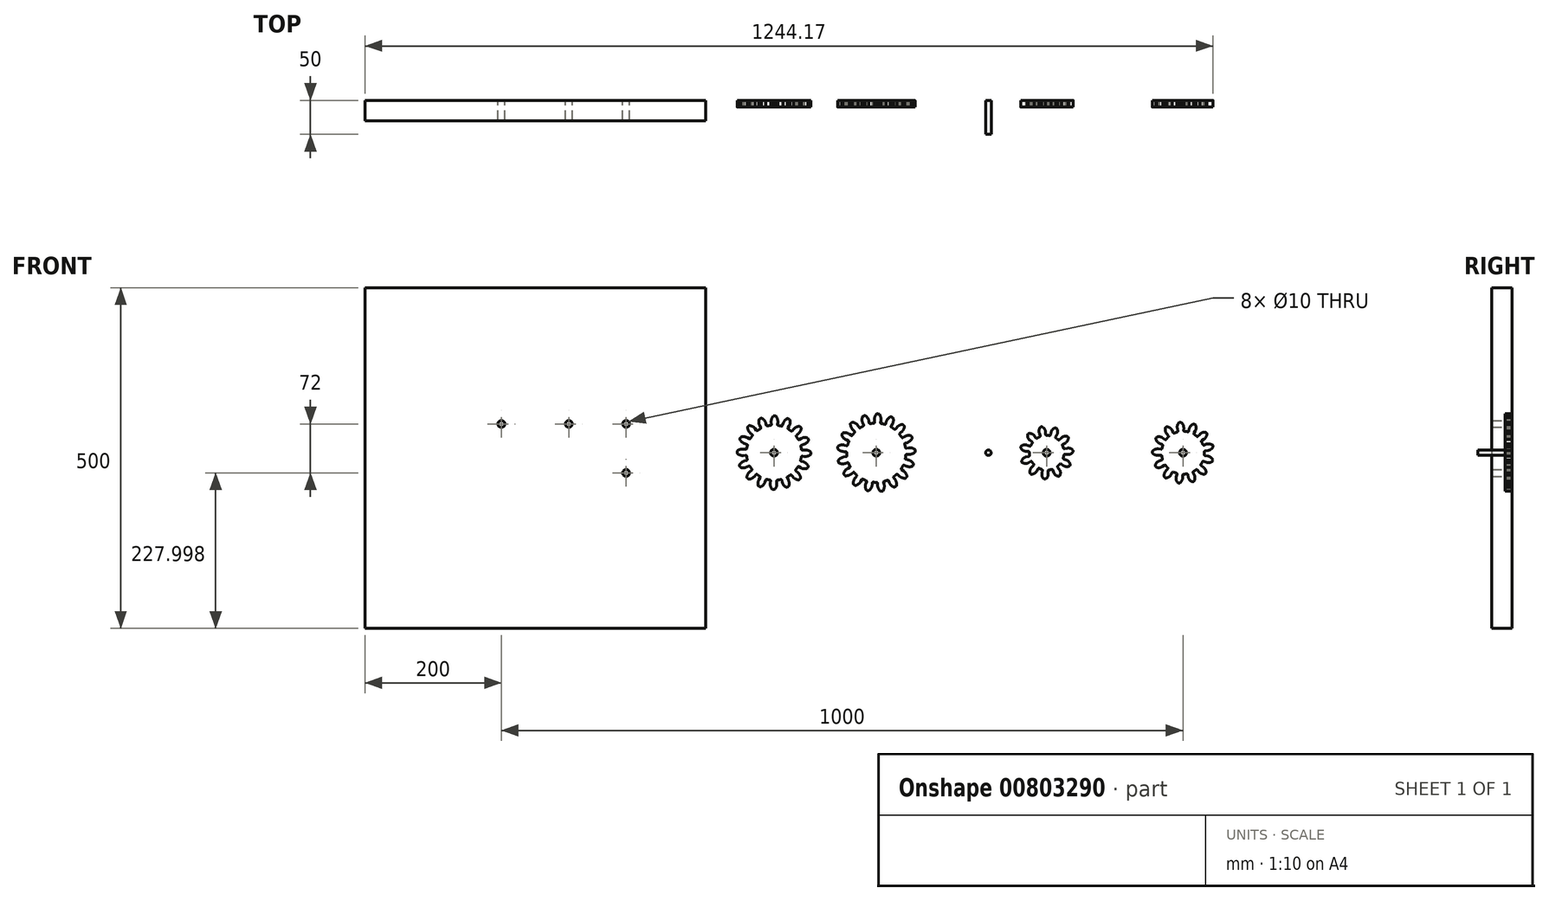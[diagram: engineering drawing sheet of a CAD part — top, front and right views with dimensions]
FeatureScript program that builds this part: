
annotation { "Feature Type Name" : "Feature", "Feature Type Description" : "" }
export const myFeature = defineFeature(function(context is Context, id is Id, definition is map)
    precondition{}
    {
        {
            var Q0;
            Q0=qCreatedBy(makeId("Front.planeOp"),FACE);
            var sketch = newSketch(context, id + "F0", { "sketchPlane" : qUnion([Q0])});
            skArc(sketch, "E0.0", {"start": v(-18.3, 50.8) * mm, "mid": v(-19.94, 50.18) * mm, "end": v(-21.55, 49.51) * mm});
            skPoint(sketch, "E1", {"position": v(11.62, 45) * mm});
            skArc(sketch, "E2", {"start": v(21.97, 38.92) * mm, "mid": v(23.56, 43.79) * mm, "end": v(22.98, 48.87) * mm});
            skPoint(sketch, "E3", {"position": v(22.98, 48.87) * mm});
            skPoint(sketch, "E4", {"position": v(22.17, 39.28) * mm});
            skLineSegment(sketch, "E5", {"start": v(22.17, 39.28) * mm, "end": v(20.49, 36.3) * mm});
            skPoint(sketch, "E6.visualSharp", {"position": v(19.9, 35.27) * mm});
            skArc(sketch, "E6.filletArc", {"start": v(20.49, 36.3) * mm, "mid": v(20.37, 35.4) * mm, "end": v(20.91, 34.68) * mm});
            skArc(sketch, "E7.1.0", {"start": v(5.4, 44.37) * mm, "mid": v(5, 49.47) * mm, "end": v(2.53, 53.94) * mm});
            skLineSegment(sketch, "E7.1.1", {"start": v(5.45, 44.77) * mm, "end": v(5.04, 41.38) * mm});
            skArc(sketch, "E7.1.2", {"start": v(5.04, 41.38) * mm, "mid": v(5.27, 40.5) * mm, "end": v(6.05, 40.05) * mm});
            skArc(sketch, "E7.2.0", {"start": v(-12, 43.06) * mm, "mid": v(-14.3, 47.62) * mm, "end": v(-18.3, 50.8) * mm});
            skLineSegment(sketch, "E7.2.1", {"start": v(-12.1, 43.45) * mm, "end": v(-11.18, 40.15) * mm});
            skArc(sketch, "E7.2.2", {"start": v(-11.18, 40.15) * mm, "mid": v(-10.63, 39.44) * mm, "end": v(-9.74, 39.31) * mm});
            skArc(sketch, "E7.3.0", {"start": v(-27.56, 35.2) * mm, "mid": v(-31.44, 38.52) * mm, "end": v(-36.35, 39.93) * mm});
            skLineSegment(sketch, "E7.3.1", {"start": v(-27.8, 35.51) * mm, "end": v(-25.7, 32.82) * mm});
            skArc(sketch, "E7.3.2", {"start": v(-25.7, 32.82) * mm, "mid": v(-24.91, 32.37) * mm, "end": v(-24.04, 32.6) * mm});
            skArc(sketch, "E7.4.0", {"start": v(-38.92, 21.97) * mm, "mid": v(-43.79, 23.56) * mm, "end": v(-48.87, 22.98) * mm});
            skLineSegment(sketch, "E7.4.1", {"start": v(-39.28, 22.17) * mm, "end": v(-36.3, 20.49) * mm});
            skArc(sketch, "E7.4.2", {"start": v(-36.3, 20.49) * mm, "mid": v(-35.4, 20.37) * mm, "end": v(-34.68, 20.91) * mm});
            skArc(sketch, "E7.5.0", {"start": v(-44.37, 5.4) * mm, "mid": v(-49.47, 5) * mm, "end": v(-53.94, 2.53) * mm});
            skLineSegment(sketch, "E7.5.1", {"start": v(-44.77, 5.45) * mm, "end": v(-41.38, 5.04) * mm});
            skArc(sketch, "E7.5.2", {"start": v(-41.38, 5.04) * mm, "mid": v(-40.5, 5.27) * mm, "end": v(-40.05, 6.05) * mm});
            skArc(sketch, "E7.6.0", {"start": v(-43.06, -12) * mm, "mid": v(-47.62, -14.3) * mm, "end": v(-50.8, -18.3) * mm});
            skLineSegment(sketch, "E7.6.1", {"start": v(-43.45, -12.1) * mm, "end": v(-40.15, -11.18) * mm});
            skArc(sketch, "E7.6.2", {"start": v(-40.15, -11.18) * mm, "mid": v(-39.44, -10.63) * mm, "end": v(-39.31, -9.74) * mm});
            skArc(sketch, "E7.7.0", {"start": v(-35.2, -27.56) * mm, "mid": v(-38.52, -31.44) * mm, "end": v(-39.93, -36.35) * mm});
            skLineSegment(sketch, "E7.7.1", {"start": v(-35.51, -27.8) * mm, "end": v(-32.82, -25.7) * mm});
            skArc(sketch, "E7.7.2", {"start": v(-32.82, -25.7) * mm, "mid": v(-32.37, -24.91) * mm, "end": v(-32.6, -24.04) * mm});
            skArc(sketch, "E7.8.0", {"start": v(-21.97, -38.92) * mm, "mid": v(-23.56, -43.79) * mm, "end": v(-22.98, -48.87) * mm});
            skLineSegment(sketch, "E7.8.1", {"start": v(-22.17, -39.28) * mm, "end": v(-20.49, -36.3) * mm});
            skArc(sketch, "E7.8.2", {"start": v(-20.49, -36.3) * mm, "mid": v(-20.37, -35.4) * mm, "end": v(-20.91, -34.68) * mm});
            skArc(sketch, "E7.9.0", {"start": v(-5.4, -44.37) * mm, "mid": v(-5, -49.47) * mm, "end": v(-2.53, -53.94) * mm});
            skLineSegment(sketch, "E7.9.1", {"start": v(-5.45, -44.77) * mm, "end": v(-5.04, -41.38) * mm});
            skArc(sketch, "E7.9.2", {"start": v(-5.04, -41.38) * mm, "mid": v(-5.27, -40.5) * mm, "end": v(-6.05, -40.05) * mm});
            skArc(sketch, "E7.10.0", {"start": v(12, -43.06) * mm, "mid": v(14.3, -47.62) * mm, "end": v(18.3, -50.8) * mm});
            skLineSegment(sketch, "E7.10.1", {"start": v(12.1, -43.45) * mm, "end": v(11.18, -40.15) * mm});
            skArc(sketch, "E7.10.2", {"start": v(11.18, -40.15) * mm, "mid": v(10.63, -39.44) * mm, "end": v(9.74, -39.31) * mm});
            skArc(sketch, "E7.11.0", {"start": v(27.56, -35.2) * mm, "mid": v(31.44, -38.52) * mm, "end": v(36.35, -39.93) * mm});
            skLineSegment(sketch, "E7.11.1", {"start": v(27.8, -35.51) * mm, "end": v(25.7, -32.82) * mm});
            skArc(sketch, "E7.11.2", {"start": v(25.7, -32.82) * mm, "mid": v(24.91, -32.37) * mm, "end": v(24.04, -32.6) * mm});
            skArc(sketch, "E7.12.0", {"start": v(38.92, -21.97) * mm, "mid": v(43.79, -23.56) * mm, "end": v(48.87, -22.98) * mm});
            skLineSegment(sketch, "E7.12.1", {"start": v(39.28, -22.17) * mm, "end": v(36.3, -20.49) * mm});
            skArc(sketch, "E7.12.2", {"start": v(36.3, -20.49) * mm, "mid": v(35.4, -20.37) * mm, "end": v(34.68, -20.91) * mm});
            skArc(sketch, "E7.13.0", {"start": v(44.37, -5.4) * mm, "mid": v(49.47, -5) * mm, "end": v(53.94, -2.53) * mm});
            skLineSegment(sketch, "E7.13.1", {"start": v(44.77, -5.45) * mm, "end": v(41.38, -5.04) * mm});
            skArc(sketch, "E7.13.2", {"start": v(41.38, -5.04) * mm, "mid": v(40.5, -5.27) * mm, "end": v(40.05, -6.05) * mm});
            skArc(sketch, "E7.14.0", {"start": v(43.06, 12) * mm, "mid": v(47.62, 14.3) * mm, "end": v(50.8, 18.3) * mm});
            skLineSegment(sketch, "E7.14.1", {"start": v(43.45, 12.1) * mm, "end": v(40.15, 11.18) * mm});
            skArc(sketch, "E7.14.2", {"start": v(40.15, 11.18) * mm, "mid": v(39.44, 10.63) * mm, "end": v(39.31, 9.74) * mm});
            skArc(sketch, "E7.15.0", {"start": v(35.2, 27.56) * mm, "mid": v(38.52, 31.44) * mm, "end": v(39.93, 36.35) * mm});
            skLineSegment(sketch, "E7.15.1", {"start": v(35.51, 27.8) * mm, "end": v(32.82, 25.7) * mm});
            skArc(sketch, "E7.15.2", {"start": v(32.82, 25.7) * mm, "mid": v(32.37, 24.91) * mm, "end": v(32.6, 24.04) * mm});
            skPoint(sketch, "E8", {"position": v(30.99, 36.66) * mm});
            skLineSegment(sketch, "E9", {"start": v(0, 0) * mm, "end": v(34.43, 33.45) * mm, "construction": true});
            skArc(sketch, "E10.MirrorCS", {"start": v(28.56, 34.38) * mm, "mid": v(32.54, 37.6) * mm, "end": v(37.5, 38.86) * mm});
            skLineSegment(sketch, "E11.MirrorCS", {"start": v(28.82, 34.7) * mm, "end": v(26.64, 32.06) * mm});
            skArc(sketch, "E12.MirrorCS", {"start": v(26.64, 32.06) * mm, "mid": v(25.84, 31.63) * mm, "end": v(24.97, 31.88) * mm});
            skArc(sketch, "E13.1.0", {"start": v(13.23, 42.7) * mm, "mid": v(15.68, 47.18) * mm, "end": v(19.77, 50.25) * mm});
            skLineSegment(sketch, "E13.1.1", {"start": v(13.35, 43.08) * mm, "end": v(12.34, 39.81) * mm});
            skArc(sketch, "E13.1.2", {"start": v(12.34, 39.81) * mm, "mid": v(11.77, 39.12) * mm, "end": v(10.87, 39.01) * mm});
            skArc(sketch, "E13.2.0", {"start": v(-4.11, 44.5) * mm, "mid": v(-3.57, 49.6) * mm, "end": v(-0.97, 54) * mm});
            skLineSegment(sketch, "E13.2.1", {"start": v(-4.15, 44.91) * mm, "end": v(-3.83, 41.5) * mm});
            skArc(sketch, "E13.2.2", {"start": v(-3.83, 41.5) * mm, "mid": v(-4.1, 40.64) * mm, "end": v(-4.88, 40.2) * mm});
            skArc(sketch, "E14.2.3.0", {"start": v(-20.83, 39.54) * mm, "mid": v(-22.28, 44.45) * mm, "end": v(-21.55, 49.51) * mm});
            skLineSegment(sketch, "E14.4.3.0", {"start": v(-21.02, 39.9) * mm, "end": v(-19.43, 36.88) * mm});
            skArc(sketch, "E14.7.3.0", {"start": v(-19.43, 36.88) * mm, "mid": v(-19.34, 35.98) * mm, "end": v(-19.9, 35.27) * mm});
            skArc(sketch, "E14.2.4.0", {"start": v(-34.38, 28.56) * mm, "mid": v(-37.6, 32.54) * mm, "end": v(-38.86, 37.5) * mm});
            skLineSegment(sketch, "E14.4.4.0", {"start": v(-34.7, 28.82) * mm, "end": v(-32.06, 26.64) * mm});
            skArc(sketch, "E14.7.4.0", {"start": v(-32.06, 26.64) * mm, "mid": v(-31.63, 25.84) * mm, "end": v(-31.88, 24.97) * mm});
            skArc(sketch, "E14.2.5.0", {"start": v(-42.7, 13.23) * mm, "mid": v(-47.18, 15.68) * mm, "end": v(-50.25, 19.77) * mm});
            skLineSegment(sketch, "E14.4.5.0", {"start": v(-43.08, 13.35) * mm, "end": v(-39.81, 12.34) * mm});
            skArc(sketch, "E14.7.5.0", {"start": v(-39.81, 12.34) * mm, "mid": v(-39.12, 11.77) * mm, "end": v(-39.01, 10.87) * mm});
            skArc(sketch, "E14.2.6.0", {"start": v(-44.5, -4.11) * mm, "mid": v(-49.6, -3.57) * mm, "end": v(-54, -0.97) * mm});
            skLineSegment(sketch, "E14.4.6.0", {"start": v(-44.91, -4.15) * mm, "end": v(-41.5, -3.83) * mm});
            skArc(sketch, "E14.7.6.0", {"start": v(-41.5, -3.83) * mm, "mid": v(-40.64, -4.1) * mm, "end": v(-40.2, -4.88) * mm});
            skArc(sketch, "E14.2.7.0", {"start": v(-39.54, -20.83) * mm, "mid": v(-44.45, -22.28) * mm, "end": v(-49.51, -21.55) * mm});
            skLineSegment(sketch, "E14.4.7.0", {"start": v(-39.9, -21.02) * mm, "end": v(-36.88, -19.43) * mm});
            skArc(sketch, "E14.7.7.0", {"start": v(-36.88, -19.43) * mm, "mid": v(-35.98, -19.34) * mm, "end": v(-35.27, -19.9) * mm});
            skArc(sketch, "E14.2.8.0", {"start": v(-28.56, -34.38) * mm, "mid": v(-32.54, -37.6) * mm, "end": v(-37.5, -38.86) * mm});
            skLineSegment(sketch, "E14.4.8.0", {"start": v(-28.82, -34.7) * mm, "end": v(-26.64, -32.06) * mm});
            skArc(sketch, "E14.7.8.0", {"start": v(-26.64, -32.06) * mm, "mid": v(-25.84, -31.63) * mm, "end": v(-24.97, -31.88) * mm});
            skArc(sketch, "E14.2.9.0", {"start": v(-13.23, -42.7) * mm, "mid": v(-15.68, -47.18) * mm, "end": v(-19.77, -50.25) * mm});
            skLineSegment(sketch, "E14.4.9.0", {"start": v(-13.35, -43.08) * mm, "end": v(-12.34, -39.81) * mm});
            skArc(sketch, "E14.7.9.0", {"start": v(-12.34, -39.81) * mm, "mid": v(-11.77, -39.12) * mm, "end": v(-10.87, -39.01) * mm});
            skArc(sketch, "E14.2.10.0", {"start": v(4.11, -44.5) * mm, "mid": v(3.57, -49.6) * mm, "end": v(0.97, -54) * mm});
            skLineSegment(sketch, "E14.4.10.0", {"start": v(4.15, -44.91) * mm, "end": v(3.83, -41.5) * mm});
            skArc(sketch, "E14.7.10.0", {"start": v(3.83, -41.5) * mm, "mid": v(4.1, -40.64) * mm, "end": v(4.88, -40.2) * mm});
            skArc(sketch, "E14.2.11.0", {"start": v(20.83, -39.54) * mm, "mid": v(22.28, -44.45) * mm, "end": v(21.55, -49.51) * mm});
            skLineSegment(sketch, "E14.4.11.0", {"start": v(21.02, -39.9) * mm, "end": v(19.43, -36.88) * mm});
            skArc(sketch, "E14.7.11.0", {"start": v(19.43, -36.88) * mm, "mid": v(19.34, -35.98) * mm, "end": v(19.9, -35.27) * mm});
            skArc(sketch, "E14.2.12.0", {"start": v(34.38, -28.56) * mm, "mid": v(37.6, -32.54) * mm, "end": v(38.86, -37.5) * mm});
            skLineSegment(sketch, "E14.4.12.0", {"start": v(34.7, -28.82) * mm, "end": v(32.06, -26.64) * mm});
            skArc(sketch, "E14.7.12.0", {"start": v(32.06, -26.64) * mm, "mid": v(31.63, -25.84) * mm, "end": v(31.88, -24.97) * mm});
            skArc(sketch, "E14.2.13.0", {"start": v(42.7, -13.23) * mm, "mid": v(47.18, -15.68) * mm, "end": v(50.25, -19.77) * mm});
            skLineSegment(sketch, "E14.4.13.0", {"start": v(43.08, -13.35) * mm, "end": v(39.81, -12.34) * mm});
            skArc(sketch, "E14.7.13.0", {"start": v(39.81, -12.34) * mm, "mid": v(39.12, -11.77) * mm, "end": v(39.01, -10.87) * mm});
            skArc(sketch, "E14.2.14.0", {"start": v(44.5, 4.11) * mm, "mid": v(49.6, 3.57) * mm, "end": v(54, 0.97) * mm});
            skLineSegment(sketch, "E14.4.14.0", {"start": v(44.91, 4.15) * mm, "end": v(41.5, 3.83) * mm});
            skArc(sketch, "E14.7.14.0", {"start": v(41.5, 3.83) * mm, "mid": v(40.64, 4.1) * mm, "end": v(40.2, 4.88) * mm});
            skArc(sketch, "E14.2.15.0", {"start": v(39.54, 20.83) * mm, "mid": v(44.45, 22.28) * mm, "end": v(49.51, 21.55) * mm});
            skLineSegment(sketch, "E14.4.15.0", {"start": v(39.9, 21.02) * mm, "end": v(36.88, 19.43) * mm});
            skArc(sketch, "E14.7.15.0", {"start": v(36.88, 19.43) * mm, "mid": v(35.98, 19.34) * mm, "end": v(35.27, 19.9) * mm});
            skArc(sketch, "E15", {"start": v(-19.9, 35.27) * mm, "mid": v(-22.01, 34) * mm, "end": v(-24.04, 32.6) * mm});
            skArc(sketch, "E16.trimOffspring", {"start": v(-36.35, 39.93) * mm, "mid": v(-37.63, 38.73) * mm, "end": v(-38.86, 37.5) * mm});
            skArc(sketch, "E17.trimOffspring", {"start": v(-48.87, 22.98) * mm, "mid": v(-49.58, 21.39) * mm, "end": v(-50.25, 19.77) * mm});
            skArc(sketch, "E18.trimOffspring", {"start": v(-53.94, 2.53) * mm, "mid": v(-54, 0.78) * mm, "end": v(-54, -0.97) * mm});
            skArc(sketch, "E19.trimOffspring", {"start": v(-50.8, -18.3) * mm, "mid": v(-50.18, -19.94) * mm, "end": v(-49.51, -21.55) * mm});
            skArc(sketch, "E20.trimOffspring", {"start": v(-39.93, -36.35) * mm, "mid": v(-38.73, -37.63) * mm, "end": v(-37.5, -38.86) * mm});
            skArc(sketch, "E21.trimOffspring", {"start": v(-22.98, -48.87) * mm, "mid": v(-21.39, -49.58) * mm, "end": v(-19.77, -50.25) * mm});
            skArc(sketch, "E22.trimOffspring", {"start": v(-2.53, -53.94) * mm, "mid": v(-0.78, -54) * mm, "end": v(0.97, -54) * mm});
            skArc(sketch, "E23.trimOffspring", {"start": v(18.3, -50.8) * mm, "mid": v(19.94, -50.18) * mm, "end": v(21.55, -49.51) * mm});
            skArc(sketch, "E24.trimOffspring", {"start": v(36.35, -39.93) * mm, "mid": v(37.63, -38.73) * mm, "end": v(38.86, -37.5) * mm});
            skArc(sketch, "E25.trimOffspring", {"start": v(48.87, -22.98) * mm, "mid": v(49.58, -21.39) * mm, "end": v(50.25, -19.77) * mm});
            skArc(sketch, "E26.trimOffspring", {"start": v(53.94, -2.53) * mm, "mid": v(54, -0.78) * mm, "end": v(54, 0.97) * mm});
            skArc(sketch, "E27.trimOffspring", {"start": v(50.8, 18.3) * mm, "mid": v(50.18, 19.94) * mm, "end": v(49.51, 21.55) * mm});
            skArc(sketch, "E28.trimOffspring", {"start": v(39.93, 36.35) * mm, "mid": v(38.73, 37.63) * mm, "end": v(37.5, 38.86) * mm});
            skArc(sketch, "E29.trimOffspring", {"start": v(22.98, 48.87) * mm, "mid": v(21.39, 49.58) * mm, "end": v(19.77, 50.25) * mm});
            skArc(sketch, "E30.trimOffspring", {"start": v(2.53, 53.94) * mm, "mid": v(0.78, 54) * mm, "end": v(-0.97, 54) * mm});
            skArc(sketch, "E31.trimOffspring", {"start": v(-31.88, 24.97) * mm, "mid": v(-33.35, 22.99) * mm, "end": v(-34.68, 20.91) * mm});
            skArc(sketch, "E32.trimOffspring", {"start": v(-39.01, 10.87) * mm, "mid": v(-39.6, 8.48) * mm, "end": v(-40.05, 6.05) * mm});
            skArc(sketch, "E33.trimOffspring", {"start": v(-40.2, -4.88) * mm, "mid": v(-39.83, -7.32) * mm, "end": v(-39.31, -9.74) * mm});
            skArc(sketch, "E34.trimOffspring", {"start": v(-35.27, -19.9) * mm, "mid": v(-34, -22.01) * mm, "end": v(-32.6, -24.04) * mm});
            skArc(sketch, "E35.trimOffspring", {"start": v(-24.97, -31.88) * mm, "mid": v(-22.99, -33.35) * mm, "end": v(-20.91, -34.68) * mm});
            skArc(sketch, "E36.trimOffspring", {"start": v(-10.87, -39.01) * mm, "mid": v(-8.48, -39.6) * mm, "end": v(-6.05, -40.05) * mm});
            skArc(sketch, "E37.trimOffspring", {"start": v(4.88, -40.2) * mm, "mid": v(7.32, -39.83) * mm, "end": v(9.74, -39.31) * mm});
            skArc(sketch, "E38.trimOffspring", {"start": v(19.9, -35.27) * mm, "mid": v(22.01, -34) * mm, "end": v(24.04, -32.6) * mm});
            skArc(sketch, "E39.trimOffspring", {"start": v(39.01, -10.87) * mm, "mid": v(39.6, -8.48) * mm, "end": v(40.05, -6.05) * mm});
            skArc(sketch, "E40.trimOffspring", {"start": v(31.88, -24.97) * mm, "mid": v(33.35, -22.99) * mm, "end": v(34.68, -20.91) * mm});
            skArc(sketch, "E41.trimOffspring", {"start": v(40.2, 4.88) * mm, "mid": v(39.83, 7.32) * mm, "end": v(39.31, 9.74) * mm});
            skArc(sketch, "E42.trimOffspring", {"start": v(35.27, 19.9) * mm, "mid": v(34, 22.01) * mm, "end": v(32.6, 24.04) * mm});
            skArc(sketch, "E43.trimOffspring", {"start": v(24.97, 31.88) * mm, "mid": v(22.5, 33.67) * mm, "end": v(19.9, 35.27) * mm});
            skArc(sketch, "E44.trimOffspring", {"start": v(-4.88, 40.2) * mm, "mid": v(-7.32, 39.83) * mm, "end": v(-9.74, 39.31) * mm});
            skArc(sketch, "E45.trimOffspring", {"start": v(10.87, 39.01) * mm, "mid": v(8.48, 39.6) * mm, "end": v(6.05, 40.05) * mm});
            skCircle(sketch, "E46", {"center": v(0, 0) * mm, "radius": 5 * mm});
            skSolve(sketch);
        }
        {
            var Q0;
            {var subQ101=sQuery(id+"F0.wireOp",EDGE,"E0.0");Q0=makeQuery(id+"F0.imprint","IMPRINT",FACE,{"disambiguationData":[TD([[makeQuery(id+"F0.imprint","IMPRINT",EDGE,{"derivedFrom":subQ101}),1.0]])]});}
            extrude(context, id + "F1", {"entities" : qUnion([Q0]), "depth" : 10 * mm, "offsetDistance" : 25 * mm});
        }
        {
            var Q0;
            Q0=qCreatedBy(makeId("Front.planeOp"),FACE);
            var sketch = newSketch(context, id + "F2", { "sketchPlane" : qUnion([Q0])});
            skArc(sketch, "E47.0", {"start": v(174.57, 51.43) * mm, "mid": v(172.88, 52.2) * mm, "end": v(171.16, 52.93) * mm});
            skLineSegment(sketch, "E48", {"start": v(150, 74.29) * mm, "end": v(150, -92.93) * mm, "construction": true});
            skArc(sketch, "E49", {"start": v(173.55, 41.74) * mm, "mid": v(175.03, 46.48) * mm, "end": v(174.57, 51.43) * mm});
            skLineSegment(sketch, "E50", {"start": v(173.55, 41.74) * mm, "end": v(171.87, 38.75) * mm});
            skArc(sketch, "E51.filletArc", {"start": v(171.87, 38.75) * mm, "mid": v(171.77, 38) * mm, "end": v(172.23, 37.4) * mm});
            skArc(sketch, "E52.1.0", {"start": v(156.89, 47.43) * mm, "mid": v(156.54, 52.38) * mm, "end": v(154.33, 56.84) * mm});
            skArc(sketch, "E52.2.0", {"start": v(139.29, 46.71) * mm, "mid": v(137.18, 51.21) * mm, "end": v(133.5, 54.56) * mm});
            skArc(sketch, "E52.3.0", {"start": v(123.14, 39.69) * mm, "mid": v(119.54, 43.12) * mm, "end": v(114.91, 44.92) * mm});
            skArc(sketch, "E52.4.0", {"start": v(110.61, 27.3) * mm, "mid": v(106.02, 29.2) * mm, "end": v(101.05, 29.21) * mm});
            skArc(sketch, "E52.5.0", {"start": v(103.41, 11.23) * mm, "mid": v(98.44, 11.35) * mm, "end": v(93.8, 9.56) * mm});
            skArc(sketch, "E52.6.0", {"start": v(102.5, -6.36) * mm, "mid": v(97.82, -8.04) * mm, "end": v(94.15, -11.39) * mm});
            skArc(sketch, "E52.7.0", {"start": v(108, -23.09) * mm, "mid": v(104.25, -26.35) * mm, "end": v(102.03, -30.8) * mm});
            skArc(sketch, "E52.8.0", {"start": v(119.18, -36.7) * mm, "mid": v(116.86, -41.1) * mm, "end": v(116.4, -46.04) * mm});
            skArc(sketch, "E52.9.0", {"start": v(134.52, -45.35) * mm, "mid": v(133.94, -50.3) * mm, "end": v(135.3, -55.07) * mm});
            skArc(sketch, "E52.10.0", {"start": v(151.95, -47.88) * mm, "mid": v(153.2, -52.7) * mm, "end": v(156.19, -56.66) * mm});
            skArc(sketch, "E52.11.0", {"start": v(169.11, -43.95) * mm, "mid": v(172.01, -47.98) * mm, "end": v(176.24, -50.6) * mm});
            skArc(sketch, "E52.12.0", {"start": v(183.7, -34.08) * mm, "mid": v(187.86, -36.8) * mm, "end": v(192.74, -37.7) * mm});
            skArc(sketch, "E52.13.0", {"start": v(193.73, -19.6) * mm, "mid": v(198.6, -20.63) * mm, "end": v(203.48, -19.72) * mm});
            skArc(sketch, "E52.14.0", {"start": v(197.86, -2.48) * mm, "mid": v(202.77, -1.68) * mm, "end": v(207, 0.93) * mm});
            skArc(sketch, "E52.15.0", {"start": v(195.52, 14.98) * mm, "mid": v(199.8, 17.5) * mm, "end": v(202.8, 21.46) * mm});
            skArc(sketch, "E52.16.0", {"start": v(187.04, 30.4) * mm, "mid": v(190.13, 34.3) * mm, "end": v(191.5, 39.08) * mm});
            skLineSegment(sketch, "E53.1.0", {"start": v(156.89, 47.43) * mm, "end": v(156.4, 44.03) * mm});
            skArc(sketch, "E53.1.1", {"start": v(156.4, 44.03) * mm, "mid": v(156.58, 43.3) * mm, "end": v(157.22, 42.9) * mm});
            skLineSegment(sketch, "E53.2.0", {"start": v(139.29, 46.71) * mm, "end": v(140.06, 43.36) * mm});
            skArc(sketch, "E53.2.1", {"start": v(140.06, 43.36) * mm, "mid": v(140.5, 42.75) * mm, "end": v(141.23, 42.6) * mm});
            skLineSegment(sketch, "E53.3.0", {"start": v(123.14, 39.69) * mm, "end": v(125.06, 36.84) * mm});
            skArc(sketch, "E53.3.1", {"start": v(125.06, 36.84) * mm, "mid": v(125.7, 36.42) * mm, "end": v(126.43, 36.56) * mm});
            skLineSegment(sketch, "E53.4.0", {"start": v(110.61, 27.3) * mm, "end": v(113.44, 25.35) * mm});
            skArc(sketch, "E53.4.1", {"start": v(113.44, 25.35) * mm, "mid": v(114.18, 25.18) * mm, "end": v(114.82, 25.58) * mm});
            skLineSegment(sketch, "E53.5.0", {"start": v(103.41, 11.23) * mm, "end": v(106.75, 10.43) * mm});
            skArc(sketch, "E53.5.1", {"start": v(106.75, 10.43) * mm, "mid": v(107.5, 10.54) * mm, "end": v(107.95, 11.15) * mm});
            skLineSegment(sketch, "E53.6.0", {"start": v(102.5, -6.36) * mm, "end": v(105.9, -5.9) * mm});
            skArc(sketch, "E53.6.1", {"start": v(105.9, -5.9) * mm, "mid": v(106.56, -5.52) * mm, "end": v(106.77, -4.8) * mm});
            skLineSegment(sketch, "E53.7.0", {"start": v(108, -23.09) * mm, "end": v(111.01, -21.43) * mm});
            skArc(sketch, "E53.7.1", {"start": v(111.01, -21.43) * mm, "mid": v(111.49, -20.84) * mm, "end": v(111.42, -20.1) * mm});
            skLineSegment(sketch, "E53.8.0", {"start": v(119.18, -36.7) * mm, "end": v(121.39, -34.07) * mm});
            skArc(sketch, "E53.8.1", {"start": v(121.39, -34.07) * mm, "mid": v(121.62, -33.35) * mm, "end": v(121.28, -32.67) * mm});
            skLineSegment(sketch, "E53.9.0", {"start": v(134.52, -45.35) * mm, "end": v(135.63, -42.1) * mm});
            skArc(sketch, "E53.9.1", {"start": v(135.63, -42.1) * mm, "mid": v(135.58, -41.35) * mm, "end": v(135.02, -40.84) * mm});
            skLineSegment(sketch, "E53.10.0", {"start": v(151.95, -47.88) * mm, "end": v(151.8, -44.45) * mm});
            skArc(sketch, "E53.10.1", {"start": v(151.8, -44.45) * mm, "mid": v(151.5, -43.77) * mm, "end": v(150.79, -43.5) * mm});
            skLineSegment(sketch, "E53.11.0", {"start": v(169.11, -43.95) * mm, "end": v(167.74, -40.8) * mm});
            skArc(sketch, "E53.11.1", {"start": v(167.74, -40.8) * mm, "mid": v(167.2, -40.27) * mm, "end": v(166.45, -40.27) * mm});
            skLineSegment(sketch, "E53.12.0", {"start": v(183.7, -34.08) * mm, "end": v(181.28, -31.63) * mm});
            skArc(sketch, "E53.12.1", {"start": v(181.28, -31.63) * mm, "mid": v(180.59, -31.34) * mm, "end": v(179.88, -31.61) * mm});
            skLineSegment(sketch, "E53.13.0", {"start": v(193.73, -19.6) * mm, "end": v(190.6, -18.2) * mm});
            skArc(sketch, "E53.13.1", {"start": v(190.6, -18.2) * mm, "mid": v(189.84, -18.17) * mm, "end": v(189.28, -18.68) * mm});
            skLineSegment(sketch, "E53.14.0", {"start": v(197.86, -2.48) * mm, "end": v(194.43, -2.3) * mm});
            skArc(sketch, "E53.14.1", {"start": v(194.43, -2.3) * mm, "mid": v(193.72, -2.55) * mm, "end": v(193.38, -3.23) * mm});
            skLineSegment(sketch, "E53.15.0", {"start": v(195.52, 14.98) * mm, "end": v(192.26, 13.9) * mm});
            skArc(sketch, "E53.15.1", {"start": v(192.26, 13.9) * mm, "mid": v(191.69, 13.41) * mm, "end": v(191.62, 12.66) * mm});
            skLineSegment(sketch, "E53.16.0", {"start": v(187.04, 30.4) * mm, "end": v(184.39, 28.23) * mm});
            skArc(sketch, "E53.16.1", {"start": v(184.39, 28.23) * mm, "mid": v(184.03, 27.57) * mm, "end": v(184.23, 26.84) * mm});
            skArc(sketch, "E54.MirrorCS", {"start": v(191.6, 23.8) * mm, "mid": v(196.34, 25.29) * mm, "end": v(201.3, 24.86) * mm});
            skLineSegment(sketch, "E55.MirrorCS", {"start": v(191.6, 23.8) * mm, "end": v(188.62, 22.09) * mm});
            skArc(sketch, "E56.MirrorCS", {"start": v(188.62, 22.09) * mm, "mid": v(187.87, 21.99) * mm, "end": v(187.27, 22.44) * mm});
            skArc(sketch, "E57.1.0", {"start": v(180.2, 37.21) * mm, "mid": v(184.08, 40.32) * mm, "end": v(188.85, 41.71) * mm});
            skLineSegment(sketch, "E57.1.1", {"start": v(180.2, 37.21) * mm, "end": v(178.03, 34.55) * mm});
            skArc(sketch, "E57.1.2", {"start": v(178.03, 34.55) * mm, "mid": v(177.37, 34.18) * mm, "end": v(176.64, 34.39) * mm});
            skArc(sketch, "E57.2.0", {"start": v(164.72, 45.6) * mm, "mid": v(167.2, 49.9) * mm, "end": v(171.16, 52.93) * mm});
            skLineSegment(sketch, "E57.2.1", {"start": v(164.72, 45.6) * mm, "end": v(163.66, 42.34) * mm});
            skArc(sketch, "E57.2.2", {"start": v(163.66, 42.34) * mm, "mid": v(163.18, 41.76) * mm, "end": v(162.42, 41.69) * mm});
            skArc(sketch, "E57.3.0", {"start": v(147.25, 47.85) * mm, "mid": v(148.02, 52.75) * mm, "end": v(150.6, 57) * mm});
            skLineSegment(sketch, "E57.3.1", {"start": v(147.25, 47.85) * mm, "end": v(147.44, 44.42) * mm});
            skArc(sketch, "E57.3.2", {"start": v(147.44, 44.42) * mm, "mid": v(147.2, 43.7) * mm, "end": v(146.52, 43.36) * mm});
            skArc(sketch, "E57.4.0", {"start": v(130.15, 43.62) * mm, "mid": v(129.1, 48.48) * mm, "end": v(129.98, 53.37) * mm});
            skLineSegment(sketch, "E57.4.1", {"start": v(130.15, 43.62) * mm, "end": v(131.57, 40.5) * mm});
            skArc(sketch, "E57.4.2", {"start": v(131.57, 40.5) * mm, "mid": v(131.6, 39.74) * mm, "end": v(131.1, 39.18) * mm});
            skArc(sketch, "E57.5.0", {"start": v(115.73, 33.5) * mm, "mid": v(113, 37.65) * mm, "end": v(112.05, 42.53) * mm});
            skLineSegment(sketch, "E57.5.1", {"start": v(115.73, 33.5) * mm, "end": v(118.19, 31.1) * mm});
            skArc(sketch, "E57.5.2", {"start": v(118.19, 31.1) * mm, "mid": v(118.49, 30.4) * mm, "end": v(118.22, 29.7) * mm});
            skArc(sketch, "E57.6.0", {"start": v(105.94, 18.86) * mm, "mid": v(101.9, 21.74) * mm, "end": v(99.25, 25.95) * mm});
            skLineSegment(sketch, "E57.6.1", {"start": v(105.94, 18.86) * mm, "end": v(109.1, 17.51) * mm});
            skArc(sketch, "E57.6.2", {"start": v(109.1, 17.51) * mm, "mid": v(109.63, 16.97) * mm, "end": v(109.64, 16.22) * mm});
            skArc(sketch, "E57.7.0", {"start": v(102.1, 1.67) * mm, "mid": v(97.29, 2.9) * mm, "end": v(93.3, 5.86) * mm});
            skLineSegment(sketch, "E57.7.1", {"start": v(102.1, 1.67) * mm, "end": v(105.54, 1.55) * mm});
            skArc(sketch, "E57.7.2", {"start": v(105.54, 1.55) * mm, "mid": v(106.23, 1.24) * mm, "end": v(106.5, 0.54) * mm});
            skArc(sketch, "E57.8.0", {"start": v(104.73, -15.74) * mm, "mid": v(99.8, -16.34) * mm, "end": v(95.01, -15.01) * mm});
            skLineSegment(sketch, "E57.8.1", {"start": v(104.73, -15.74) * mm, "end": v(107.98, -14.61) * mm});
            skArc(sketch, "E57.8.2", {"start": v(107.98, -14.61) * mm, "mid": v(108.73, -14.65) * mm, "end": v(109.25, -15.2) * mm});
            skArc(sketch, "E57.9.0", {"start": v(113.48, -31.03) * mm, "mid": v(109.1, -33.37) * mm, "end": v(104.15, -33.86) * mm});
            skLineSegment(sketch, "E57.9.1", {"start": v(113.48, -31.03) * mm, "end": v(116.1, -28.8) * mm});
            skArc(sketch, "E57.9.2", {"start": v(116.1, -28.8) * mm, "mid": v(116.81, -28.57) * mm, "end": v(117.5, -28.9) * mm});
            skArc(sketch, "E57.10.0", {"start": v(127.15, -42.13) * mm, "mid": v(123.91, -45.9) * mm, "end": v(119.48, -48.14) * mm});
            skLineSegment(sketch, "E57.10.1", {"start": v(127.15, -42.13) * mm, "end": v(128.8, -39.1) * mm});
            skArc(sketch, "E57.10.2", {"start": v(128.8, -39.1) * mm, "mid": v(129.38, -38.63) * mm, "end": v(130.13, -38.7) * mm});
            skArc(sketch, "E57.11.0", {"start": v(143.91, -47.54) * mm, "mid": v(142.25, -52.22) * mm, "end": v(138.93, -55.91) * mm});
            skLineSegment(sketch, "E57.11.1", {"start": v(143.91, -47.54) * mm, "end": v(144.35, -44.13) * mm});
            skArc(sketch, "E57.11.2", {"start": v(144.35, -44.13) * mm, "mid": v(144.72, -43.47) * mm, "end": v(145.45, -43.26) * mm});
            skArc(sketch, "E57.12.0", {"start": v(161.5, -46.52) * mm, "mid": v(161.64, -51.5) * mm, "end": v(159.88, -56.14) * mm});
            skLineSegment(sketch, "E57.12.1", {"start": v(161.5, -46.52) * mm, "end": v(160.67, -43.2) * mm});
            skArc(sketch, "E57.12.2", {"start": v(160.67, -43.2) * mm, "mid": v(160.78, -42.44) * mm, "end": v(161.38, -41.98) * mm});
            skArc(sketch, "E57.13.0", {"start": v(177.53, -39.23) * mm, "mid": v(179.46, -43.8) * mm, "end": v(179.49, -48.78) * mm});
            skLineSegment(sketch, "E57.13.1", {"start": v(177.53, -39.23) * mm, "end": v(175.56, -36.42) * mm});
            skArc(sketch, "E57.13.2", {"start": v(175.56, -36.42) * mm, "mid": v(175.39, -35.68) * mm, "end": v(175.78, -35.04) * mm});
            skArc(sketch, "E57.14.0", {"start": v(189.84, -26.64) * mm, "mid": v(193.3, -30.21) * mm, "end": v(195.12, -34.83) * mm});
            skLineSegment(sketch, "E57.14.1", {"start": v(189.84, -26.64) * mm, "end": v(186.99, -24.73) * mm});
            skArc(sketch, "E57.14.2", {"start": v(186.99, -24.73) * mm, "mid": v(186.56, -24.1) * mm, "end": v(186.7, -23.36) * mm});
            skArc(sketch, "E57.15.0", {"start": v(196.77, -10.45) * mm, "mid": v(201.28, -12.53) * mm, "end": v(204.65, -16.18) * mm});
            skLineSegment(sketch, "E57.15.1", {"start": v(196.77, -10.45) * mm, "end": v(193.42, -9.7) * mm});
            skArc(sketch, "E57.15.2", {"start": v(193.42, -9.7) * mm, "mid": v(192.8, -9.27) * mm, "end": v(192.66, -8.52) * mm});
            skArc(sketch, "E57.16.0", {"start": v(197.39, 7.16) * mm, "mid": v(202.35, 6.84) * mm, "end": v(206.8, 4.65) * mm});
            skLineSegment(sketch, "E57.16.1", {"start": v(197.39, 7.16) * mm, "end": v(194, 6.64) * mm});
            skArc(sketch, "E57.16.2", {"start": v(194, 6.64) * mm, "mid": v(193.26, 6.82) * mm, "end": v(192.86, 7.46) * mm});
            skArc(sketch, "E58.trimOffspring", {"start": v(191.5, 39.08) * mm, "mid": v(190.2, 40.42) * mm, "end": v(188.85, 41.71) * mm});
            skArc(sketch, "E59.trimOffspring", {"start": v(202.8, 21.46) * mm, "mid": v(202.08, 23.17) * mm, "end": v(201.3, 24.86) * mm});
            skArc(sketch, "E60.trimOffspring", {"start": v(207, 0.93) * mm, "mid": v(206.93, 2.8) * mm, "end": v(206.8, 4.65) * mm});
            skArc(sketch, "E61.trimOffspring", {"start": v(203.48, -19.72) * mm, "mid": v(204.1, -17.96) * mm, "end": v(204.65, -16.18) * mm});
            skArc(sketch, "E62.trimOffspring", {"start": v(192.74, -37.7) * mm, "mid": v(193.96, -36.29) * mm, "end": v(195.12, -34.83) * mm});
            skArc(sketch, "E63.trimOffspring", {"start": v(176.24, -50.6) * mm, "mid": v(177.88, -49.72) * mm, "end": v(179.49, -48.78) * mm});
            skArc(sketch, "E64.trimOffspring", {"start": v(135.3, -55.07) * mm, "mid": v(137.1, -55.52) * mm, "end": v(138.93, -55.91) * mm});
            skArc(sketch, "E65.trimOffspring", {"start": v(156.19, -56.66) * mm, "mid": v(158.04, -56.43) * mm, "end": v(159.88, -56.14) * mm});
            skArc(sketch, "E66.trimOffspring", {"start": v(116.4, -46.04) * mm, "mid": v(117.92, -47.12) * mm, "end": v(119.48, -48.14) * mm});
            skArc(sketch, "E67.trimOffspring", {"start": v(102.03, -30.8) * mm, "mid": v(103.07, -32.35) * mm, "end": v(104.15, -33.86) * mm});
            skArc(sketch, "E68.trimOffspring", {"start": v(94.15, -11.39) * mm, "mid": v(94.55, -13.2) * mm, "end": v(95.01, -15.01) * mm});
            skArc(sketch, "E69.trimOffspring", {"start": v(93.8, 9.56) * mm, "mid": v(93.52, 7.71) * mm, "end": v(93.3, 5.86) * mm});
            skArc(sketch, "E70.trimOffspring", {"start": v(101.05, 29.21) * mm, "mid": v(100.12, 27.6) * mm, "end": v(99.25, 25.95) * mm});
            skArc(sketch, "E71.trimOffspring", {"start": v(114.91, 44.92) * mm, "mid": v(113.46, 43.75) * mm, "end": v(112.05, 42.53) * mm});
            skArc(sketch, "E72.trimOffspring", {"start": v(133.5, 54.56) * mm, "mid": v(131.73, 54) * mm, "end": v(129.98, 53.37) * mm});
            skArc(sketch, "E73.trimOffspring", {"start": v(154.33, 56.84) * mm, "mid": v(152.17, 56.96) * mm, "end": v(150, 57) * mm});
            skArc(sketch, "E74", {"start": v(192.86, 7.46) * mm, "mid": v(192.32, 10.08) * mm, "end": v(191.62, 12.66) * mm});
            skArc(sketch, "E75.trimOffspring", {"start": v(192.66, -8.52) * mm, "mid": v(193.1, -5.89) * mm, "end": v(193.38, -3.23) * mm});
            skArc(sketch, "E76.trimOffspring", {"start": v(186.7, -23.36) * mm, "mid": v(188.06, -21.06) * mm, "end": v(189.28, -18.68) * mm});
            skArc(sketch, "E77.trimOffspring", {"start": v(175.78, -35.04) * mm, "mid": v(177.88, -33.39) * mm, "end": v(179.88, -31.61) * mm});
            skArc(sketch, "E78.trimOffspring", {"start": v(161.38, -41.98) * mm, "mid": v(163.94, -41.2) * mm, "end": v(166.45, -40.27) * mm});
            skArc(sketch, "E79.trimOffspring", {"start": v(145.45, -43.26) * mm, "mid": v(148.11, -43.46) * mm, "end": v(150.79, -43.5) * mm});
            skArc(sketch, "E80.trimOffspring", {"start": v(130.13, -38.7) * mm, "mid": v(132.54, -39.84) * mm, "end": v(135.02, -40.84) * mm});
            skArc(sketch, "E81.trimOffspring", {"start": v(109.25, -15.2) * mm, "mid": v(110.26, -17.68) * mm, "end": v(111.42, -20.1) * mm});
            skArc(sketch, "E82.trimOffspring", {"start": v(117.5, -28.9) * mm, "mid": v(119.33, -30.85) * mm, "end": v(121.28, -32.67) * mm});
            skArc(sketch, "E83.trimOffspring", {"start": v(106.5, 0.54) * mm, "mid": v(106.55, -2.13) * mm, "end": v(106.77, -4.8) * mm});
            skArc(sketch, "E84.trimOffspring", {"start": v(109.64, 16.22) * mm, "mid": v(108.72, 13.7) * mm, "end": v(107.95, 11.15) * mm});
            skArc(sketch, "E85.trimOffspring", {"start": v(118.22, 29.7) * mm, "mid": v(116.46, 27.7) * mm, "end": v(114.82, 25.58) * mm});
            skArc(sketch, "E86.trimOffspring", {"start": v(131.1, 39.18) * mm, "mid": v(128.72, 37.94) * mm, "end": v(126.43, 36.56) * mm});
            skArc(sketch, "E87.trimOffspring", {"start": v(146.52, 43.36) * mm, "mid": v(143.87, 43.07) * mm, "end": v(141.23, 42.6) * mm});
            skArc(sketch, "E88.trimOffspring", {"start": v(162.42, 41.69) * mm, "mid": v(159.84, 42.37) * mm, "end": v(157.22, 42.9) * mm});
            skArc(sketch, "E89.trimOffspring", {"start": v(176.64, 34.39) * mm, "mid": v(174.48, 35.96) * mm, "end": v(172.23, 37.4) * mm});
            skArc(sketch, "E90.trimOffspring", {"start": v(187.27, 22.44) * mm, "mid": v(185.82, 24.69) * mm, "end": v(184.23, 26.84) * mm});
            skCircle(sketch, "E91", {"center": v(150, 0) * mm, "radius": 5 * mm});
            skSolve(sketch);
        }
        {
            var Q0;
            Q0=makeQuery(id+"F2.imprint","IMPRINT",FACE,{"disambiguationData":[TD([[makeQuery(id+"F2.imprint","IMPRINT",EDGE,{"derivedFrom":sQuery(id+"F2.wireOp",EDGE,"E47.0")}),1.0]])]});
            extrude(context, id + "F3", {"entities" : qUnion([Q0]), "depth" : 10 * mm, "offsetDistance" : 25 * mm});
        }
        {
            var Q0;
            Q0=qCreatedBy(makeId("Front.planeOp"),FACE);
            var sketch = newSketch(context, id + "F4", { "sketchPlane" : qUnion([Q0])});
            skLineSegment(sketch, "E92.bottom", {"start": v(-100, 242.29) * mm, "end": v(-600, 242.29) * mm});
            skLineSegment(sketch, "E92.top", {"start": v(-100, -257.71) * mm, "end": v(-600, -257.71) * mm});
            skLineSegment(sketch, "E92.left", {"start": v(-100, 242.29) * mm, "end": v(-100, -257.71) * mm});
            skLineSegment(sketch, "E92.right", {"start": v(-600, 242.29) * mm, "end": v(-600, -257.71) * mm});
            skCircle(sketch, "E93", {"center": v(-400, 42.29) * mm, "radius": 5 * mm});
            skCircle(sketch, "E94", {"center": v(-301, 42.29) * mm, "radius": 5 * mm});
            skCircle(sketch, "E95", {"center": v(-217, 42.29) * mm, "radius": 5 * mm});
            skCircle(sketch, "E96", {"center": v(-217, -29.71) * mm, "radius": 5 * mm});
            skSolve(sketch);
        }
        {
            var Q0;
            Q0=makeQuery(id+"F4.imprint","IMPRINT",FACE,{"disambiguationData":[TD([[makeQuery(id+"F4.imprint","IMPRINT",EDGE,{"derivedFrom":sQuery(id+"F4.wireOp",EDGE,"E92.bottom")}),1.0]])]});
            extrude(context, id + "F5", {"entities" : qUnion([Q0]), "depth" : 30 * mm, "offsetDistance" : 25 * mm});
        }
        {
            var Q0;
            Q0=qCreatedBy(makeId("Front.planeOp"),FACE);
            var sketch = newSketch(context, id + "F6", { "sketchPlane" : qUnion([Q0])});
            skCircle(sketch, "E97", {"center": v(314.57, 0) * mm, "radius": 4 * mm});
            skSolve(sketch);
        }
        {
            var Q0;
            Q0=makeQuery(id+"F6.imprint","IMPRINT",FACE,{"disambiguationData":[TD([[makeQuery(id+"F6.imprint","IMPRINT",EDGE,{"derivedFrom":sQuery(id+"F6.wireOp",EDGE,"E97")}),1.0]])]});
            extrude(context, id + "F7", {"entities" : qUnion([Q0]), "depth" : 50 * mm, "offsetDistance" : 25 * mm});
        }
        {
            var Q0;
            Q0=qCreatedBy(makeId("Front.planeOp"),FACE);
            var sketch = newSketch(context, id + "F8", { "sketchPlane" : qUnion([Q0])});
            skArc(sketch, "E98.0", {"start": v(392.37, 38.25) * mm, "mid": v(391.92, 38.15) * mm, "end": v(391.48, 38.06) * mm});
            skLineSegment(sketch, "E99", {"start": v(400, 46.58) * mm, "end": v(400, -66.83) * mm, "construction": true});
            skArc(sketch, "E100", {"start": v(415.1, 26.76) * mm, "mid": v(416.2, 31.67) * mm, "end": v(414.26, 36.3) * mm});
            skLineSegment(sketch, "E101", {"start": v(413.1, 23.23) * mm, "end": v(415.24, 27) * mm});
            skArc(sketch, "E102.filletArc", {"start": v(413.1, 23.23) * mm, "mid": v(413, 22.34) * mm, "end": v(413.52, 21.62) * mm});
            skArc(sketch, "E103.1.0", {"start": v(398.24, 30.68) * mm, "mid": v(396.51, 35.4) * mm, "end": v(392.37, 38.25) * mm});
            skLineSegment(sketch, "E103.1.1", {"start": v(398.47, 26.63) * mm, "end": v(398.22, 30.96) * mm});
            skArc(sketch, "E103.1.2", {"start": v(398.47, 26.63) * mm, "mid": v(398.85, 25.82) * mm, "end": v(399.68, 25.5) * mm});
            skArc(sketch, "E103.2.0", {"start": v(381.93, 24.85) * mm, "mid": v(377.93, 27.9) * mm, "end": v(372.9, 28.05) * mm});
            skLineSegment(sketch, "E103.2.1", {"start": v(384.32, 21.57) * mm, "end": v(381.77, 25.08) * mm});
            skArc(sketch, "E103.2.2", {"start": v(384.32, 21.57) * mm, "mid": v(385.07, 21.1) * mm, "end": v(385.95, 21.28) * mm});
            skArc(sketch, "E103.3.0", {"start": v(371.36, 11.14) * mm, "mid": v(366.35, 11.53) * mm, "end": v(362.04, 8.95) * mm});
            skLineSegment(sketch, "E103.3.1", {"start": v(375.14, 9.67) * mm, "end": v(371.1, 11.24) * mm});
            skArc(sketch, "E103.3.2", {"start": v(375.14, 9.67) * mm, "mid": v(376.04, 9.68) * mm, "end": v(376.67, 10.3) * mm});
            skArc(sketch, "E103.4.0", {"start": v(369.89, -6.11) * mm, "mid": v(365.46, -8.49) * mm, "end": v(363.23, -13) * mm});
            skLineSegment(sketch, "E103.4.1", {"start": v(373.86, -5.3) * mm, "end": v(369.6, -6.17) * mm});
            skArc(sketch, "E103.4.2", {"start": v(373.86, -5.3) * mm, "mid": v(374.6, -4.81) * mm, "end": v(374.8, -3.94) * mm});
            skArc(sketch, "E103.5.0", {"start": v(377.97, -21.42) * mm, "mid": v(375.53, -25.82) * mm, "end": v(376.1, -30.81) * mm});
            skLineSegment(sketch, "E103.5.1", {"start": v(380.88, -18.6) * mm, "end": v(377.77, -21.62) * mm});
            skArc(sketch, "E103.5.2", {"start": v(380.88, -18.6) * mm, "mid": v(381.24, -17.78) * mm, "end": v(380.94, -16.94) * mm});
            skArc(sketch, "E103.6.0", {"start": v(393.05, -29.93) * mm, "mid": v(393.37, -34.95) * mm, "end": v(396.55, -38.85) * mm});
            skLineSegment(sketch, "E103.6.1", {"start": v(393.97, -25.98) * mm, "end": v(392.98, -30.2) * mm});
            skArc(sketch, "E103.6.2", {"start": v(393.97, -25.98) * mm, "mid": v(393.83, -25.1) * mm, "end": v(393.12, -24.55) * mm});
            skArc(sketch, "E103.7.0", {"start": v(410.33, -28.94) * mm, "mid": v(413.32, -32.98) * mm, "end": v(418.1, -34.55) * mm});
            skLineSegment(sketch, "E103.7.1", {"start": v(408.97, -25.12) * mm, "end": v(410.43, -29.2) * mm});
            skArc(sketch, "E103.7.2", {"start": v(408.97, -25.12) * mm, "mid": v(408.38, -24.45) * mm, "end": v(407.49, -24.38) * mm});
            skArc(sketch, "E103.8.0", {"start": v(424.34, -18.76) * mm, "mid": v(429.04, -20.55) * mm, "end": v(433.9, -19.28) * mm});
            skLineSegment(sketch, "E103.8.1", {"start": v(421.13, -16.28) * mm, "end": v(424.56, -18.93) * mm});
            skArc(sketch, "E103.8.2", {"start": v(421.13, -16.28) * mm, "mid": v(420.27, -16.04) * mm, "end": v(419.48, -16.46) * mm});
            skArc(sketch, "E103.9.0", {"start": v(430.62, -2.62) * mm, "mid": v(435.54, -1.59) * mm, "end": v(438.94, 2.11) * mm});
            skLineSegment(sketch, "E103.9.1", {"start": v(426.58, -2.28) * mm, "end": v(430.9, -2.65) * mm});
            skArc(sketch, "E103.9.2", {"start": v(426.58, -2.28) * mm, "mid": v(425.72, -2.54) * mm, "end": v(425.28, -3.31) * mm});
            skArc(sketch, "E103.10.0", {"start": v(427.17, 14.35) * mm, "mid": v(430.75, 17.88) * mm, "end": v(431.62, 22.83) * mm});
            skLineSegment(sketch, "E103.10.1", {"start": v(423.59, 12.45) * mm, "end": v(427.42, 14.48) * mm});
            skArc(sketch, "E103.10.2", {"start": v(423.59, 12.45) * mm, "mid": v(423, 11.77) * mm, "end": v(423.06, 10.88) * mm});
            skArc(sketch, "E104.MirrorCS", {"start": v(421.67, 21.8) * mm, "mid": v(426.09, 24.18) * mm, "end": v(431.08, 23.56) * mm});
            skLineSegment(sketch, "E105.MirrorCS", {"start": v(418.8, 18.91) * mm, "end": v(421.86, 22) * mm});
            skArc(sketch, "E106.MirrorCS", {"start": v(418.8, 18.91) * mm, "mid": v(417.99, 18.56) * mm, "end": v(417.15, 18.87) * mm});
            skArc(sketch, "E107", {"start": v(378.88, 14.29) * mm, "mid": v(377.69, 12.35) * mm, "end": v(376.67, 10.3) * mm});
            skArc(sketch, "E108.1.0", {"start": v(406.45, 30.04) * mm, "mid": v(408.87, 34.45) * mm, "end": v(413.4, 36.62) * mm});
            skLineSegment(sketch, "E108.1.1", {"start": v(405.6, 26.08) * mm, "end": v(406.5, 30.32) * mm});
            skArc(sketch, "E108.1.2", {"start": v(405.6, 26.08) * mm, "mid": v(405.1, 25.34) * mm, "end": v(404.22, 25.15) * mm});
            skArc(sketch, "E108.2.0", {"start": v(389.18, 28.76) * mm, "mid": v(388.84, 33.78) * mm, "end": v(391.48, 38.06) * mm});
            skLineSegment(sketch, "E108.2.1", {"start": v(390.6, 24.96) * mm, "end": v(389.08, 29.02) * mm});
            skArc(sketch, "E108.2.2", {"start": v(390.6, 24.96) * mm, "mid": v(390.59, 24.07) * mm, "end": v(389.96, 23.44) * mm});
            skArc(sketch, "E108.3.0", {"start": v(375.35, 18.34) * mm, "mid": v(372.35, 22.38) * mm, "end": v(372.25, 27.4) * mm});
            skLineSegment(sketch, "E108.3.1", {"start": v(378.6, 15.92) * mm, "end": v(375.12, 18.51) * mm});
            skArc(sketch, "E108.3.2", {"start": v(378.6, 15.92) * mm, "mid": v(379.07, 15.16) * mm, "end": v(378.88, 14.29) * mm});
            skArc(sketch, "E108.4.0", {"start": v(369.34, 2.1) * mm, "mid": v(364.64, 3.88) * mm, "end": v(361.84, 8.06) * mm});
            skLineSegment(sketch, "E108.4.1", {"start": v(373.39, 1.83) * mm, "end": v(369.06, 2.12) * mm});
            skArc(sketch, "E108.4.2", {"start": v(373.39, 1.83) * mm, "mid": v(374.2, 1.44) * mm, "end": v(374.5, 0.6) * mm});
            skArc(sketch, "E108.5.0", {"start": v(373.07, -14.8) * mm, "mid": v(368.16, -15.85) * mm, "end": v(363.54, -13.85) * mm});
            skLineSegment(sketch, "E108.5.1", {"start": v(376.63, -12.85) * mm, "end": v(372.83, -14.94) * mm});
            skArc(sketch, "E108.5.2", {"start": v(376.63, -12.85) * mm, "mid": v(377.51, -12.74) * mm, "end": v(378.23, -13.28) * mm});
            skArc(sketch, "E108.6.0", {"start": v(385.35, -27.01) * mm, "mid": v(381.78, -30.55) * mm, "end": v(376.82, -31.36) * mm});
            skLineSegment(sketch, "E108.6.1", {"start": v(387.28, -23.45) * mm, "end": v(385.22, -27.26) * mm});
            skArc(sketch, "E108.6.2", {"start": v(387.28, -23.45) * mm, "mid": v(387.97, -22.88) * mm, "end": v(388.86, -22.94) * mm});
            skArc(sketch, "E108.7.0", {"start": v(402.28, -30.64) * mm, "mid": v(401.2, -35.55) * mm, "end": v(397.46, -38.92) * mm});
            skLineSegment(sketch, "E108.7.1", {"start": v(401.98, -26.6) * mm, "end": v(402.3, -30.92) * mm});
            skArc(sketch, "E108.7.2", {"start": v(401.98, -26.6) * mm, "mid": v(402.25, -25.75) * mm, "end": v(403.03, -25.32) * mm});
            skArc(sketch, "E108.8.0", {"start": v(418.49, -24.55) * mm, "mid": v(420.22, -29.26) * mm, "end": v(418.9, -34.11) * mm});
            skLineSegment(sketch, "E108.8.1", {"start": v(416.05, -21.3) * mm, "end": v(418.65, -24.77) * mm});
            skArc(sketch, "E108.8.2", {"start": v(416.05, -21.3) * mm, "mid": v(415.81, -20.44) * mm, "end": v(416.24, -19.66) * mm});
            skArc(sketch, "E108.9.0", {"start": v(428.82, -10.66) * mm, "mid": v(432.83, -13.69) * mm, "end": v(434.34, -18.48) * mm});
            skLineSegment(sketch, "E108.9.1", {"start": v(425.02, -9.25) * mm, "end": v(429.09, -10.75) * mm});
            skArc(sketch, "E108.9.2", {"start": v(425.02, -9.25) * mm, "mid": v(424.36, -8.65) * mm, "end": v(424.3, -7.76) * mm});
            skArc(sketch, "E108.10.0", {"start": v(430, 6.62) * mm, "mid": v(435.02, 6.24) * mm, "end": v(438.88, 3.02) * mm});
            skLineSegment(sketch, "E108.10.1", {"start": v(426.05, 5.74) * mm, "end": v(430.28, 6.68) * mm});
            skArc(sketch, "E108.10.2", {"start": v(426.05, 5.74) * mm, "mid": v(425.17, 5.9) * mm, "end": v(424.63, 6.6) * mm});
            skArc(sketch, "E109.trimOffspring", {"start": v(389.96, 23.44) * mm, "mid": v(387.9, 22.45) * mm, "end": v(385.95, 21.28) * mm});
            skArc(sketch, "E110.trimOffspring", {"start": v(404.22, 25.15) * mm, "mid": v(401.96, 25.42) * mm, "end": v(399.68, 25.5) * mm});
            skArc(sketch, "E111.trimOffspring", {"start": v(417.15, 18.87) * mm, "mid": v(415.4, 20.33) * mm, "end": v(413.52, 21.62) * mm});
            skArc(sketch, "E112.trimOffspring", {"start": v(424.63, 6.6) * mm, "mid": v(423.94, 8.78) * mm, "end": v(423.06, 10.88) * mm});
            skArc(sketch, "E113.trimOffspring", {"start": v(424.3, -7.76) * mm, "mid": v(424.89, -5.56) * mm, "end": v(425.28, -3.31) * mm});
            skArc(sketch, "E114.trimOffspring", {"start": v(416.24, -19.66) * mm, "mid": v(417.93, -18.13) * mm, "end": v(419.48, -16.46) * mm});
            skArc(sketch, "E115.trimOffspring", {"start": v(403.03, -25.32) * mm, "mid": v(405.28, -24.95) * mm, "end": v(407.49, -24.38) * mm});
            skArc(sketch, "E116.trimOffspring", {"start": v(388.86, -22.94) * mm, "mid": v(390.96, -23.84) * mm, "end": v(393.12, -24.55) * mm});
            skArc(sketch, "E117.trimOffspring", {"start": v(378.23, -13.28) * mm, "mid": v(379.5, -15.17) * mm, "end": v(380.94, -16.94) * mm});
            skArc(sketch, "E118.trimOffspring", {"start": v(374.5, 0.6) * mm, "mid": v(374.56, -1.68) * mm, "end": v(374.8, -3.94) * mm});
            skArc(sketch, "E119.trimOffspring", {"start": v(372.9, 28.05) * mm, "mid": v(372.58, 27.73) * mm, "end": v(372.25, 27.4) * mm});
            skArc(sketch, "E120.trimOffspring", {"start": v(362.04, 8.95) * mm, "mid": v(361.94, 8.5) * mm, "end": v(361.84, 8.06) * mm});
            skArc(sketch, "E121.trimOffspring", {"start": v(363.23, -13) * mm, "mid": v(363.38, -13.43) * mm, "end": v(363.54, -13.85) * mm});
            skArc(sketch, "E122.trimOffspring", {"start": v(376.1, -30.81) * mm, "mid": v(376.45, -31.1) * mm, "end": v(376.82, -31.36) * mm});
            skArc(sketch, "E123.trimOffspring", {"start": v(396.55, -38.85) * mm, "mid": v(397, -38.88) * mm, "end": v(397.46, -38.92) * mm});
            skArc(sketch, "E124.trimOffspring", {"start": v(418.1, -34.55) * mm, "mid": v(418.5, -34.33) * mm, "end": v(418.9, -34.11) * mm});
            skArc(sketch, "E125.trimOffspring", {"start": v(433.9, -19.28) * mm, "mid": v(434.13, -18.88) * mm, "end": v(434.34, -18.48) * mm});
            skArc(sketch, "E126.trimOffspring", {"start": v(438.94, 2.11) * mm, "mid": v(438.92, 2.57) * mm, "end": v(438.88, 3.02) * mm});
            skArc(sketch, "E127.trimOffspring", {"start": v(431.62, 22.83) * mm, "mid": v(431.35, 23.2) * mm, "end": v(431.08, 23.56) * mm});
            skArc(sketch, "E128.trimOffspring", {"start": v(414.26, 36.3) * mm, "mid": v(413.83, 36.46) * mm, "end": v(413.4, 36.62) * mm});
            skCircle(sketch, "E129", {"center": v(400, 0) * mm, "radius": 5 * mm});
            skSolve(sketch);
        }
        {
            var Q0;
            Q0 = qSketchRegion(id + "F8", true);
            extrude(context, id + "F9", {"entities" : qUnion([Q0]), "depth" : 10 * mm, "offsetDistance" : 25 * mm});
        }
        {
            var Q0;
            Q0=qCreatedBy(makeId("Front.planeOp"),FACE);
            var sketch = newSketch(context, id + "F10", { "sketchPlane" : qUnion([Q0])});
            skArc(sketch, "E130.0", {"start": v(596.76, 44.88) * mm, "mid": v(595.56, 44.78) * mm, "end": v(594.36, 44.65) * mm});
            skArc(sketch, "E131.0", {"start": v(606.83, 30.75) * mm, "mid": v(604.49, 31.18) * mm, "end": v(602.11, 31.43) * mm});
            skLineSegment(sketch, "E132", {"start": v(600, 49.61) * mm, "end": v(600, -59.75) * mm, "construction": true});
            skArc(sketch, "E133", {"start": v(617.85, 31.63) * mm, "mid": v(619.19, 36.42) * mm, "end": v(618, 41.25) * mm});
            skLineSegment(sketch, "E134", {"start": v(616.06, 28.46) * mm, "end": v(618.01, 31.92) * mm});
            skArc(sketch, "E135.filletArc", {"start": v(616.06, 28.46) * mm, "mid": v(615.94, 27.57) * mm, "end": v(616.48, 26.85) * mm});
            skArc(sketch, "E136.1.0", {"start": v(601.1, 36.3) * mm, "mid": v(600.07, 41.16) * mm, "end": v(596.76, 44.88) * mm});
            skLineSegment(sketch, "E136.1.1", {"start": v(601, 32.66) * mm, "end": v(601.12, 36.63) * mm});
            skArc(sketch, "E136.1.2", {"start": v(601, 32.66) * mm, "mid": v(601.3, 31.82) * mm, "end": v(602.11, 31.43) * mm});
            skArc(sketch, "E136.2.0", {"start": v(584.11, 32.65) * mm, "mid": v(580.93, 36.48) * mm, "end": v(576.27, 38.24) * mm});
            skLineSegment(sketch, "E136.2.1", {"start": v(585.7, 29.38) * mm, "end": v(583.97, 32.95) * mm});
            skArc(sketch, "E136.2.2", {"start": v(585.7, 29.38) * mm, "mid": v(586.37, 28.78) * mm, "end": v(587.27, 28.81) * mm});
            skArc(sketch, "E136.3.0", {"start": v(570.76, 21.53) * mm, "mid": v(566.16, 23.44) * mm, "end": v(561.22, 22.83) * mm});
            skLineSegment(sketch, "E136.3.1", {"start": v(573.68, 19.37) * mm, "end": v(570.49, 21.73) * mm});
            skArc(sketch, "E136.3.2", {"start": v(573.68, 19.37) * mm, "mid": v(574.55, 19.15) * mm, "end": v(575.34, 19.6) * mm});
            skArc(sketch, "E136.4.0", {"start": v(564.1, 5.47) * mm, "mid": v(559.14, 5.03) * mm, "end": v(555.05, 2.2) * mm});
            skLineSegment(sketch, "E136.4.1", {"start": v(567.7, 4.93) * mm, "end": v(563.77, 5.52) * mm});
            skArc(sketch, "E136.4.2", {"start": v(567.7, 4.93) * mm, "mid": v(568.57, 5.13) * mm, "end": v(569.06, 5.89) * mm});
            skArc(sketch, "E136.5.0", {"start": v(565.67, -11.84) * mm, "mid": v(561.49, -14.53) * mm, "end": v(559.18, -18.94) * mm});
            skLineSegment(sketch, "E136.5.1", {"start": v(569.1, -10.65) * mm, "end": v(565.35, -11.95) * mm});
            skArc(sketch, "E136.5.2", {"start": v(569.1, -10.65) * mm, "mid": v(569.78, -10.06) * mm, "end": v(569.86, -9.17) * mm});
            skArc(sketch, "E136.6.0", {"start": v(575.1, -26.44) * mm, "mid": v(572.65, -30.77) * mm, "end": v(572.66, -35.74) * mm});
            skLineSegment(sketch, "E136.6.1", {"start": v(577.6, -23.79) * mm, "end": v(574.87, -26.68) * mm});
            skArc(sketch, "E136.6.2", {"start": v(577.6, -23.79) * mm, "mid": v(577.92, -22.95) * mm, "end": v(577.58, -22.12) * mm});
            skArc(sketch, "E136.7.0", {"start": v(590.24, -34.98) * mm, "mid": v(590.08, -39.95) * mm, "end": v(592.4, -44.35) * mm});
            skLineSegment(sketch, "E136.7.1", {"start": v(591.22, -31.48) * mm, "end": v(590.15, -35.3) * mm});
            skArc(sketch, "E136.7.2", {"start": v(591.22, -31.48) * mm, "mid": v(591.12, -30.58) * mm, "end": v(590.43, -30) * mm});
            skArc(sketch, "E136.8.0", {"start": v(607.61, -35.5) * mm, "mid": v(609.79, -39.98) * mm, "end": v(613.89, -42.8) * mm});
            skLineSegment(sketch, "E136.8.1", {"start": v(606.85, -31.95) * mm, "end": v(607.68, -35.83) * mm});
            skArc(sketch, "E136.8.2", {"start": v(606.85, -31.95) * mm, "mid": v(606.35, -31.2) * mm, "end": v(605.47, -31.02) * mm});
            skArc(sketch, "E136.9.0", {"start": v(623.24, -27.9) * mm, "mid": v(627.25, -30.86) * mm, "end": v(632.19, -31.45) * mm});
            skLineSegment(sketch, "E136.9.1", {"start": v(620.91, -25.1) * mm, "end": v(623.45, -28.16) * mm});
            skArc(sketch, "E136.9.2", {"start": v(620.91, -25.1) * mm, "mid": v(620.12, -24.68) * mm, "end": v(619.26, -24.93) * mm});
            skArc(sketch, "E136.10.0", {"start": v(633.55, -13.9) * mm, "mid": v(638.47, -14.66) * mm, "end": v(643.11, -12.89) * mm});
            skLineSegment(sketch, "E136.10.1", {"start": v(630.19, -12.51) * mm, "end": v(633.85, -14.03) * mm});
            skArc(sketch, "E136.10.2", {"start": v(630.19, -12.51) * mm, "mid": v(629.29, -12.5) * mm, "end": v(628.64, -13.12) * mm});
            skArc(sketch, "E136.11.0", {"start": v(636.17, 3.28) * mm, "mid": v(640.87, 4.9) * mm, "end": v(644.17, 8.62) * mm});
            skLineSegment(sketch, "E136.11.1", {"start": v(632.54, 2.95) * mm, "end": v(636.5, 3.3) * mm});
            skArc(sketch, "E136.11.2", {"start": v(632.54, 2.95) * mm, "mid": v(631.75, 2.54) * mm, "end": v(631.45, 1.69) * mm});
            skArc(sketch, "E136.12.0", {"start": v(630.5, 19.7) * mm, "mid": v(633.92, 23.33) * mm, "end": v(635.1, 28.16) * mm});
            skLineSegment(sketch, "E136.12.1", {"start": v(627.45, 17.74) * mm, "end": v(630.78, 19.89) * mm});
            skArc(sketch, "E136.12.2", {"start": v(627.45, 17.74) * mm, "mid": v(626.93, 17) * mm, "end": v(627.07, 16.11) * mm});
            skArc(sketch, "E137.MirrorCS", {"start": v(624.45, 26.85) * mm, "mid": v(628.58, 29.63) * mm, "end": v(633.54, 30) * mm});
            skLineSegment(sketch, "E138.MirrorCS", {"start": v(622, 24.16) * mm, "end": v(624.67, 27.1) * mm});
            skArc(sketch, "E139.MirrorCS", {"start": v(622, 24.16) * mm, "mid": v(621.2, 23.77) * mm, "end": v(620.34, 24.05) * mm});
            skArc(sketch, "E140.1.0", {"start": v(609.17, 35.14) * mm, "mid": v(611.54, 39.51) * mm, "end": v(615.76, 42.15) * mm});
            skLineSegment(sketch, "E140.1.1", {"start": v(608.25, 31.62) * mm, "end": v(609.25, 35.46) * mm});
            skArc(sketch, "E140.1.2", {"start": v(608.25, 31.62) * mm, "mid": v(607.72, 30.9) * mm, "end": v(606.83, 30.75) * mm});
            skArc(sketch, "E140.2.0", {"start": v(591.79, 35.37) * mm, "mid": v(591.85, 40.35) * mm, "end": v(594.36, 44.65) * mm});
            skLineSegment(sketch, "E140.2.1", {"start": v(592.61, 31.83) * mm, "end": v(591.71, 35.7) * mm});
            skArc(sketch, "E140.2.2", {"start": v(592.61, 31.83) * mm, "mid": v(592.47, 30.94) * mm, "end": v(591.76, 30.4) * mm});
            skArc(sketch, "E140.3.0", {"start": v(576.3, 27.5) * mm, "mid": v(574.04, 31.94) * mm, "end": v(574.26, 36.91) * mm});
            skLineSegment(sketch, "E140.3.1", {"start": v(578.67, 24.75) * mm, "end": v(576.07, 27.76) * mm});
            skArc(sketch, "E140.3.2", {"start": v(578.67, 24.75) * mm, "mid": v(578.95, 23.9) * mm, "end": v(578.57, 23.09) * mm});
            skArc(sketch, "E140.4.0", {"start": v(566.22, 13.34) * mm, "mid": v(562.16, 16.22) * mm, "end": v(560.06, 20.72) * mm});
            skLineSegment(sketch, "E140.4.1", {"start": v(569.6, 12) * mm, "end": v(565.91, 13.46) * mm});
            skArc(sketch, "E140.4.2", {"start": v(569.6, 12) * mm, "mid": v(570.26, 11.38) * mm, "end": v(570.3, 10.49) * mm});
            skArc(sketch, "E140.5.0", {"start": v(563.9, -3.89) * mm, "mid": v(558.96, -3.22) * mm, "end": v(555, -0.21) * mm});
            skLineSegment(sketch, "E140.5.1", {"start": v(567.5, -3.5) * mm, "end": v(563.56, -3.92) * mm});
            skArc(sketch, "E140.5.2", {"start": v(567.5, -3.5) * mm, "mid": v(568.37, -3.74) * mm, "end": v(568.83, -4.52) * mm});
            skArc(sketch, "E140.6.0", {"start": v(569.84, -20.22) * mm, "mid": v(565.16, -21.93) * mm, "end": v(560.25, -21.1) * mm});
            skLineSegment(sketch, "E140.6.1", {"start": v(572.86, -18.2) * mm, "end": v(569.56, -20.4) * mm});
            skArc(sketch, "E140.6.2", {"start": v(572.86, -18.2) * mm, "mid": v(573.74, -18.01) * mm, "end": v(574.5, -18.49) * mm});
            skArc(sketch, "E140.7.0", {"start": v(582.69, -31.92) * mm, "mid": v(579.34, -35.6) * mm, "end": v(574.61, -37.15) * mm});
            skLineSegment(sketch, "E140.7.1", {"start": v(584.42, -28.73) * mm, "end": v(582.53, -32.22) * mm});
            skArc(sketch, "E140.7.2", {"start": v(584.42, -28.73) * mm, "mid": v(585.11, -28.15) * mm, "end": v(586, -28.22) * mm});
            skArc(sketch, "E140.8.0", {"start": v(599.5, -36.31) * mm, "mid": v(598.25, -41.13) * mm, "end": v(594.79, -44.7) * mm});
            skLineSegment(sketch, "E140.8.1", {"start": v(599.56, -32.67) * mm, "end": v(599.5, -36.64) * mm});
            skArc(sketch, "E140.8.2", {"start": v(599.56, -32.67) * mm, "mid": v(599.9, -31.85) * mm, "end": v(600.73, -31.5) * mm});
            skArc(sketch, "E140.9.0", {"start": v(616.44, -32.38) * mm, "mid": v(617.57, -37.23) * mm, "end": v(616.16, -42) * mm});
            skLineSegment(sketch, "E140.9.1", {"start": v(614.8, -29.14) * mm, "end": v(616.59, -32.68) * mm});
            skArc(sketch, "E140.9.2", {"start": v(614.8, -29.14) * mm, "mid": v(614.71, -28.24) * mm, "end": v(615.28, -27.55) * mm});
            skArc(sketch, "E140.10.0", {"start": v(629.6, -21.03) * mm, "mid": v(632.85, -24.8) * mm, "end": v(633.82, -29.68) * mm});
            skLineSegment(sketch, "E140.10.1", {"start": v(626.64, -18.93) * mm, "end": v(629.87, -21.23) * mm});
            skArc(sketch, "E140.10.2", {"start": v(626.64, -18.93) * mm, "mid": v(626.15, -18.17) * mm, "end": v(626.33, -17.3) * mm});
            skArc(sketch, "E140.11.0", {"start": v(635.99, -4.87) * mm, "mid": v(640.62, -6.7) * mm, "end": v(643.74, -10.56) * mm});
            skLineSegment(sketch, "E140.11.1", {"start": v(632.38, -4.38) * mm, "end": v(636.32, -4.91) * mm});
            skArc(sketch, "E140.11.2", {"start": v(632.38, -4.38) * mm, "mid": v(631.6, -3.94) * mm, "end": v(631.35, -3.07) * mm});
            skArc(sketch, "E140.12.0", {"start": v(634.13, 12.41) * mm, "mid": v(639.07, 12.95) * mm, "end": v(643.64, 10.98) * mm});
            skLineSegment(sketch, "E140.12.1", {"start": v(630.7, 11.17) * mm, "end": v(634.44, 12.53) * mm});
            skArc(sketch, "E140.12.2", {"start": v(630.7, 11.17) * mm, "mid": v(629.81, 11.2) * mm, "end": v(629.19, 11.85) * mm});
            skArc(sketch, "E141.trimOffspring", {"start": v(576.27, 38.24) * mm, "mid": v(575.26, 37.59) * mm, "end": v(574.26, 36.91) * mm});
            skArc(sketch, "E142.trimOffspring", {"start": v(561.22, 22.83) * mm, "mid": v(560.63, 21.79) * mm, "end": v(560.06, 20.72) * mm});
            skArc(sketch, "E143.trimOffspring", {"start": v(555.05, 2.2) * mm, "mid": v(555.01, 1) * mm, "end": v(555, -0.21) * mm});
            skArc(sketch, "E144.trimOffspring", {"start": v(559.18, -18.94) * mm, "mid": v(559.7, -20.03) * mm, "end": v(560.25, -21.1) * mm});
            skArc(sketch, "E145.trimOffspring", {"start": v(572.66, -35.74) * mm, "mid": v(573.63, -36.46) * mm, "end": v(574.61, -37.15) * mm});
            skArc(sketch, "E146.trimOffspring", {"start": v(592.4, -44.35) * mm, "mid": v(593.6, -44.54) * mm, "end": v(594.79, -44.7) * mm});
            skArc(sketch, "E147.trimOffspring", {"start": v(613.89, -42.8) * mm, "mid": v(615.03, -42.42) * mm, "end": v(616.16, -42) * mm});
            skArc(sketch, "E148.trimOffspring", {"start": v(632.19, -31.45) * mm, "mid": v(633.02, -30.58) * mm, "end": v(633.82, -29.68) * mm});
            skArc(sketch, "E149.trimOffspring", {"start": v(643.11, -12.89) * mm, "mid": v(643.44, -11.73) * mm, "end": v(643.74, -10.56) * mm});
            skArc(sketch, "E150.trimOffspring", {"start": v(644.17, 8.62) * mm, "mid": v(643.92, 9.8) * mm, "end": v(643.64, 10.98) * mm});
            skArc(sketch, "E151.trimOffspring", {"start": v(635.1, 28.16) * mm, "mid": v(634.33, 29.1) * mm, "end": v(633.54, 30) * mm});
            skArc(sketch, "E152.trimOffspring", {"start": v(618, 41.25) * mm, "mid": v(616.88, 41.71) * mm, "end": v(615.76, 42.15) * mm});
            skArc(sketch, "E153.trimOffspring", {"start": v(591.76, 30.4) * mm, "mid": v(589.48, 29.7) * mm, "end": v(587.27, 28.81) * mm});
            skArc(sketch, "E154.trimOffspring", {"start": v(578.57, 23.09) * mm, "mid": v(576.89, 21.4) * mm, "end": v(575.34, 19.6) * mm});
            skArc(sketch, "E155.trimOffspring", {"start": v(570.3, 10.49) * mm, "mid": v(569.59, 8.21) * mm, "end": v(569.06, 5.89) * mm});
            skArc(sketch, "E156.trimOffspring", {"start": v(568.83, -4.52) * mm, "mid": v(569.26, -6.86) * mm, "end": v(569.86, -9.17) * mm});
            skArc(sketch, "E157.trimOffspring", {"start": v(574.5, -18.49) * mm, "mid": v(575.97, -20.36) * mm, "end": v(577.58, -22.12) * mm});
            skArc(sketch, "E158.trimOffspring", {"start": v(586, -28.22) * mm, "mid": v(588.18, -29.2) * mm, "end": v(590.43, -30) * mm});
            skArc(sketch, "E159.trimOffspring", {"start": v(600, -31.5) * mm, "mid": v(602.74, -31.38) * mm, "end": v(605.47, -31.02) * mm});
            skArc(sketch, "E160.trimOffspring", {"start": v(615.28, -27.55) * mm, "mid": v(617.32, -26.31) * mm, "end": v(619.26, -24.93) * mm});
            skArc(sketch, "E161.trimOffspring", {"start": v(626.33, -17.3) * mm, "mid": v(627.56, -15.25) * mm, "end": v(628.64, -13.12) * mm});
            skArc(sketch, "E162.trimOffspring", {"start": v(631.35, -3.07) * mm, "mid": v(631.5, -0.7) * mm, "end": v(631.45, 1.69) * mm});
            skArc(sketch, "E163.trimOffspring", {"start": v(629.19, 11.85) * mm, "mid": v(628.2, 14.02) * mm, "end": v(627.07, 16.11) * mm});
            skArc(sketch, "E164.trimOffspring", {"start": v(620.34, 24.05) * mm, "mid": v(618.46, 25.52) * mm, "end": v(616.48, 26.85) * mm});
            skCircle(sketch, "E165", {"center": v(600, 0) * mm, "radius": 5 * mm});
            skSolve(sketch);
        }
        {
            var Q0;
            {var subQ43=sQuery(id+"F10.wireOp",EDGE,"E130.0");Q0=makeQuery(id+"F10.imprint","IMPRINT",FACE,{"disambiguationData":[TD([[makeQuery(id+"F10.imprint","IMPRINT",EDGE,{"derivedFrom":subQ43}),1.0]])]});}
            extrude(context, id + "F11", {"entities" : qUnion([Q0]), "depth" : 10 * mm, "offsetDistance" : 25 * mm});
        }
    });
